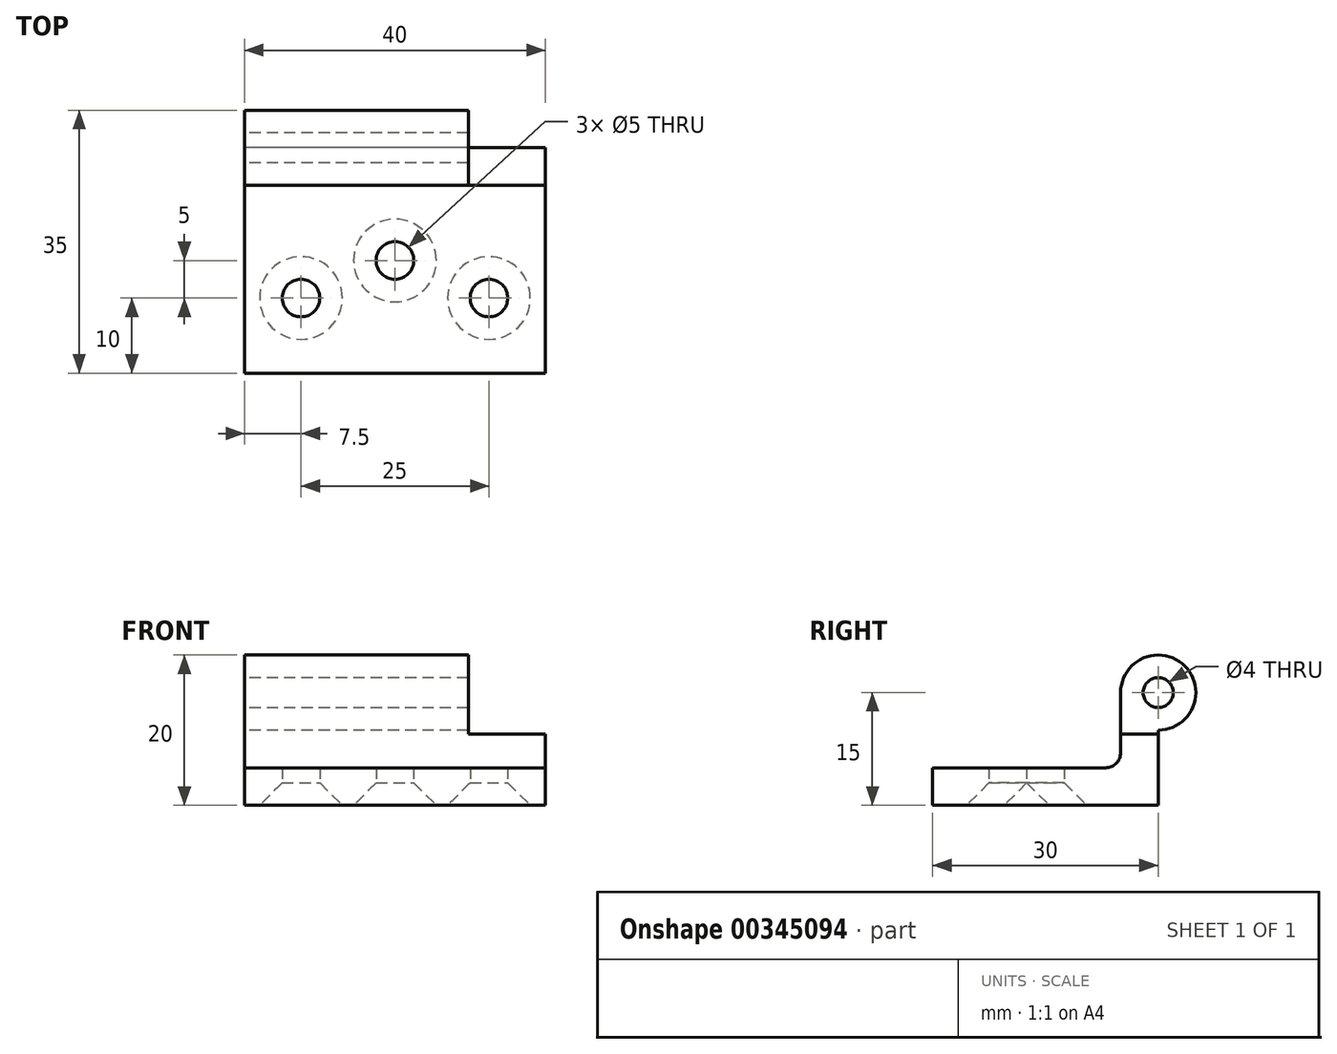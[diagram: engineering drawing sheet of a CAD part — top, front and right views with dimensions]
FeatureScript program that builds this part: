
annotation { "Feature Type Name" : "Feature", "Feature Type Description" : "" }
export const myFeature = defineFeature(function(context is Context, id is Id, definition is map)
    precondition{}
    {
        {
            var Q0;
            Q0=qCreatedBy(makeId("Right.planeOp"),FACE);
            var sketch = newSketch(context, id + "F0", { "sketchPlane" : qUnion([Q0])});
            skLineSegment(sketch, "E0", {"start": v(0, 0) * mm, "end": v(30, 0) * mm});
            skLineSegment(sketch, "E1", {"start": v(30, 0) * mm, "end": v(30, 10) * mm});
            skLineSegment(sketch, "E2", {"start": v(25, 15) * mm, "end": v(25, 5) * mm});
            skLineSegment(sketch, "E3", {"start": v(25, 5) * mm, "end": v(0, 5) * mm});
            skLineSegment(sketch, "E4", {"start": v(0, 5) * mm, "end": v(0, 0) * mm});
            skArc(sketch, "E5", {"start": v(30, 10) * mm, "mid": v(33.54, 18.54) * mm, "end": v(25, 15) * mm});
            skPoint(sketch, "E6.orphan", {"position": v(30, 12.23) * mm});
            skCircle(sketch, "E7", {"center": v(30, 15) * mm, "radius": 2 * mm});
            skSolve(sketch);
        }
        {
            var Q0;
            Q0 = qSketchRegion(id + "F0", true);
            extrude(context, id + "F1", {"entities" : qUnion([Q0]), "endBound" : BoundingType.SYMMETRIC, "depth" : 40 * mm});
        }
        {
            var Q0;
            Q0=makeQuery(id+"F1.opExtrude","SWEPT_FACE",FACE,{"disambiguationData":[OSD([sQuery(id+"F0.wireOp",EDGE,"E3")])]});
            cPlane(context, id + "F2", {"entities" : qUnion([Q0]), "cplaneType" : CPlaneType.OFFSET, "offset" : 4.5 * mm, "width" : 150 * mm, "height" : 150 * mm});
        }
        {
            var Q0;
            Q0=qCreatedBy(id+"F2.planeOp",FACE);
            var sketch = newSketch(context, id + "F3", { "sketchPlane" : qUnion([Q0])});
            skLineSegment(sketch, "E8.bottom", {"start": v(20, 25) * mm, "end": v(9.75, 25) * mm});
            skLineSegment(sketch, "E8.top", {"start": v(20, 37) * mm, "end": v(9.75, 37) * mm});
            skLineSegment(sketch, "E8.left", {"start": v(20, 25) * mm, "end": v(20, 37) * mm});
            skLineSegment(sketch, "E8.right", {"start": v(9.75, 25) * mm, "end": v(9.75, 37) * mm});
            skSolve(sketch);
        }
        {
            var Q0;
            Q0 = qSketchRegion(id + "F3", true);
            extrude(context, id + "F4", {"entities" : qUnion([Q0]), "operationType" : NewBodyOperationType.REMOVE, "endBound" : BoundingType.THROUGH_ALL, "depth" : 25 * mm});
        }
        {
            var Q0;
            Q0=makeQuery(id+"F1.opExtrude","SWEPT_EDGE",EDGE,{"disambiguationData":[OSD([sQuery(id+"F0.wireOp",EDGE,"E2"),sQuery(id+"F0.wireOp",EDGE,"E3")])]});
            fillet(context, id + "F5", {"entities" : qUnion([Q0]), "radius" : 2 * mm, "tangentPropagation" : true, "allowEdgeOverflow" : false});
        }
        {
            var Q0;
            Q0=makeQuery(id+"F1.opExtrude","SWEPT_FACE",FACE,{"disambiguationData":[OSD([sQuery(id+"F0.wireOp",EDGE,"E0")])]});
            var sketch = newSketch(context, id + "F6", { "sketchPlane" : qUnion([Q0])});
            skLineSegment(sketch, "E9", {"start": v(-12.5, -10) * mm, "end": v(12.5, -10) * mm, "construction": true});
            skLineSegment(sketch, "E10", {"start": v(0, 0) * mm, "end": v(0, -30) * mm, "construction": true});
            skPoint(sketch, "E11", {"position": v(0, -15) * mm});
            skSolve(sketch);
        }
        {
            var Q0;
            Q0=sQuery(id+"F6.wireOp",VERTEX,"E9.start");
            var Q1;
            Q1=sQuery(id+"F6.wireOp",VERTEX,"E11");
            var Q2;
            Q2=sQuery(id+"F6.wireOp",VERTEX,"E9.end");
            var Q3;
            Q3=makeQuery(id+"F1.opExtrude","SWEPT_BODY",BODY,{"disambiguationData":[OSD([sQuery(id+"F0.wireOp",EDGE,"E0"),sQuery(id+"F0.wireOp",EDGE,"E1"),sQuery(id+"F0.wireOp",EDGE,"E2"),sQuery(id+"F0.wireOp",EDGE,"E3"),sQuery(id+"F0.wireOp",EDGE,"E4"),sQuery(id+"F0.wireOp",EDGE,"E5"),sQuery(id+"F0.wireOp",EDGE,"E7")])]});
            hole(context, id + "F7", {"style" : HoleStyle.C_SINK, "endStyle" : HoleEndStyle.THROUGH, "holeDiameter" : 5 * mm, "cSinkDiameter" : 11 * mm, "cSinkAngle" : 90 * degree, "isTappedThrough" : true, "tappedDepth" : 12 * mm, "tapClearance" : 3, "startFromSketch" : true, "locations" : qUnion([Q0, Q1, Q2]), "scope" : qUnion([Q3])});
        }
    });
